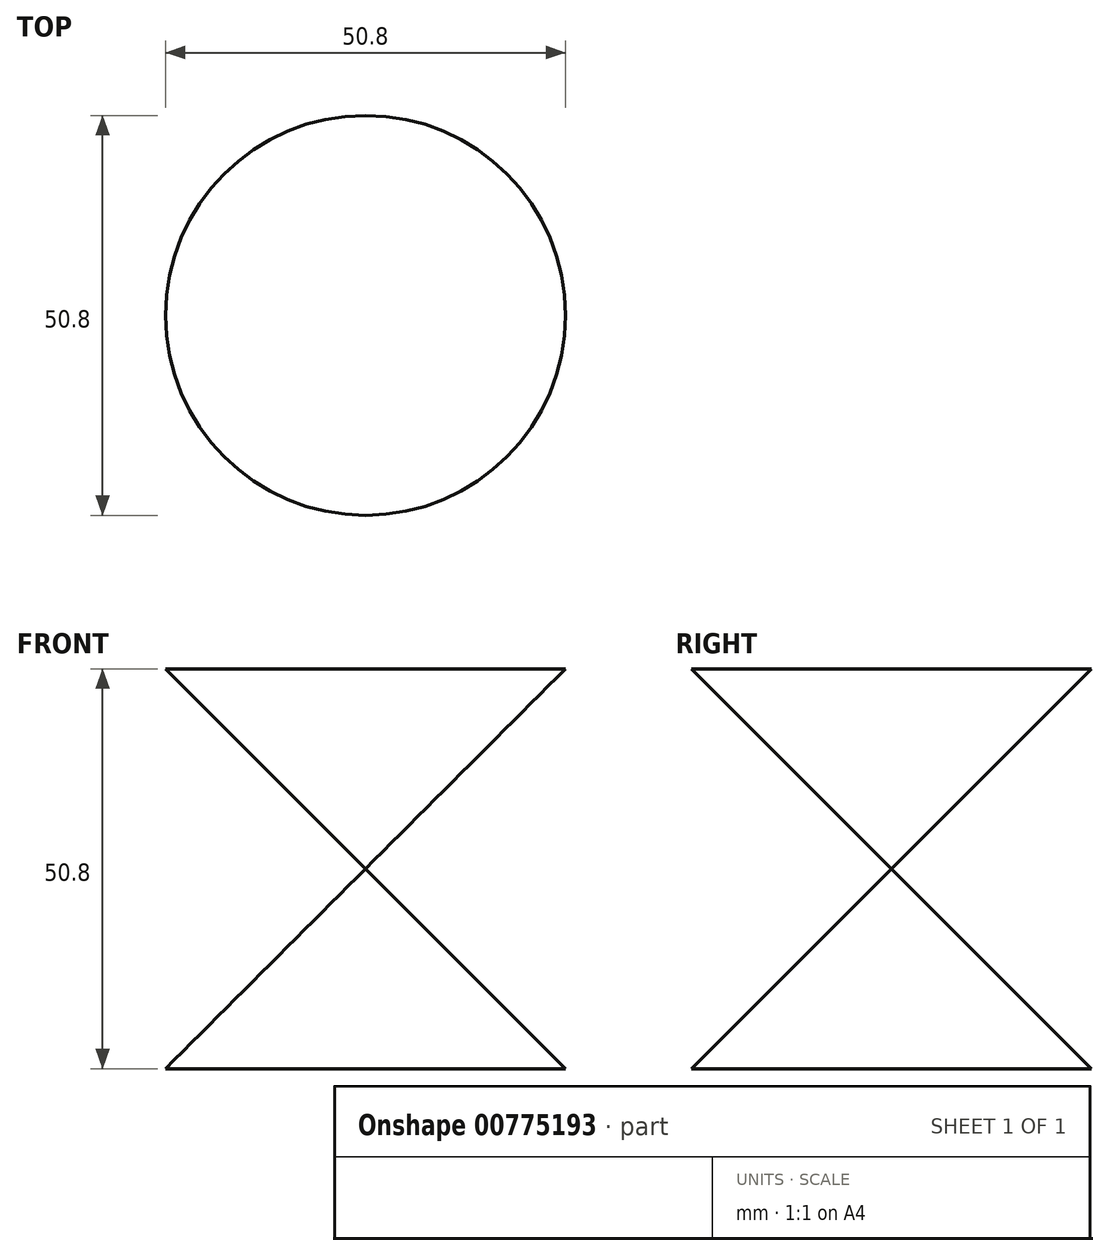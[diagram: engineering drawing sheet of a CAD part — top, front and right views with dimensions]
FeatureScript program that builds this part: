
annotation { "Feature Type Name" : "Feature", "Feature Type Description" : "" }
export const myFeature = defineFeature(function(context is Context, id is Id, definition is map)
    precondition{}
    {
        {
            var Q0;
            Q0=qCreatedBy(makeId("Front.planeOp"),FACE);
            var sketch = newSketch(context, id + "F0", { "sketchPlane" : qUnion([Q0])});
            skLineSegment(sketch, "E0", {"start": v(25.4, 25.4) * mm, "end": v(0, 0) * mm});
            skLineSegment(sketch, "E1", {"start": v(0, 0) * mm, "end": v(0, -25.4) * mm});
            skLineSegment(sketch, "E2", {"start": v(0, 0) * mm, "end": v(-25.4, -25.4) * mm});
            skLineSegment(sketch, "E3", {"start": v(0, 0) * mm, "end": v(0, 25.4) * mm});
            skSolve(sketch);
        }
        {
            var Q0;
            Q0=sQuery(id+"F0.wireOp",EDGE,"E0");
            var Q1;
            Q1=sQuery(id+"F0.wireOp",EDGE,"E1");
            revolve(context, id + "F1", {"bodyType" : ToolBodyType.SURFACE, "surfaceOperationType" : NewSurfaceOperationType.NEW, "surfaceEntities" : qUnion([Q0]), "axis" : qUnion([Q1]), "revolveType" : RevolveType.FULL});
        }
        {
            var Q0;
            Q0=sQuery(id+"F0.wireOp",EDGE,"E2");
            var Q1;
            Q1=sQuery(id+"F0.wireOp",EDGE,"E1");
            revolve(context, id + "F2", {"bodyType" : ToolBodyType.SURFACE, "surfaceOperationType" : NewSurfaceOperationType.NEW, "surfaceEntities" : qUnion([Q0]), "axis" : qUnion([Q1]), "revolveType" : RevolveType.FULL});
        }
    });
